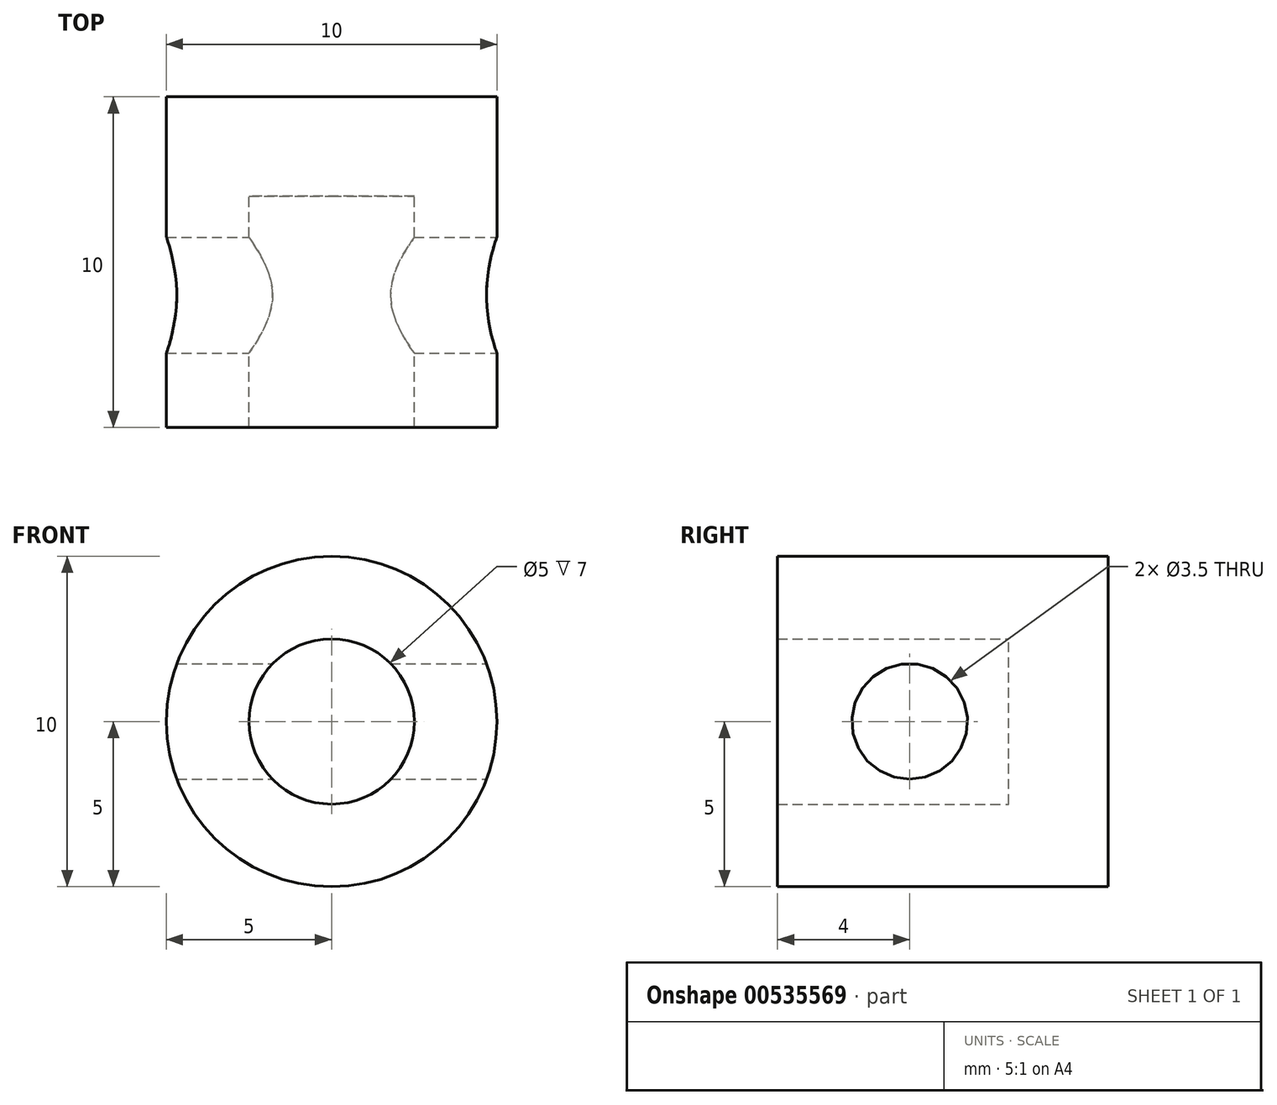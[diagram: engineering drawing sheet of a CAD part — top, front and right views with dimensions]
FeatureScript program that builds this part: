
annotation { "Feature Type Name" : "Feature", "Feature Type Description" : "" }
export const myFeature = defineFeature(function(context is Context, id is Id, definition is map)
    precondition{}
    {
        {
            var Q0;
            Q0=qCreatedBy(makeId("Front.planeOp"),FACE);
            var sketch = newSketch(context, id + "F0", { "sketchPlane" : qUnion([Q0])});
            skCircle(sketch, "E0", {"center": v(0, 0) * mm, "radius": 2.5 * mm});
            skCircle(sketch, "E1", {"center": v(0, 0) * mm, "radius": 5 * mm});
            skSolve(sketch);
        }
        {
            var Q0;
            Q0 = qSketchRegion(id + "F0", true);
            extrude(context, id + "F1", {"entities" : qUnion([Q0]), "depth" : 7 * mm, "offsetDistance" : 25 * mm});
        }
        {
            var Q0;
            Q0=qCreatedBy(makeId("Front.planeOp"),FACE);
            var sketch = newSketch(context, id + "F2", { "sketchPlane" : qUnion([Q0])});
            skCircle(sketch, "E2", {"center": v(0, 0) * mm, "radius": 5 * mm});
            skSolve(sketch);
        }
        {
            var Q0;
            Q0 = qSketchRegion(id + "F2", true);
            extrude(context, id + "F3", {"entities" : qUnion([Q0]), "operationType" : NewBodyOperationType.ADD, "oppositeDirection" : true, "depth" : 3 * mm, "offsetDistance" : 25 * mm});
        }
        {
            var Q0;
            Q0=qCreatedBy(makeId("Right.planeOp"),FACE);
            var sketch = newSketch(context, id + "F4", { "sketchPlane" : qUnion([Q0])});
            skCircle(sketch, "E3", {"center": v(-3, 0) * mm, "radius": 1.75 * mm});
            skSolve(sketch);
        }
        {
            var Q0;
            Q0 = qSketchRegion(id + "F4", true);
            extrude(context, id + "F5", {"entities" : qUnion([Q0]), "operationType" : NewBodyOperationType.REMOVE, "oppositeDirection" : true, "depth" : 25 * mm, "offsetDistance" : 25 * mm, "symmetric" : true});
        }
    });
